# Revit family: Haworth_Planes_ConferenceDesk_Rectangle_AP_PRELIMINARY
name_source: partatom
category: Furniture
units: mm (PartAtom-declared; Revit-internal decimal feet)

## family parameters
Always vertical = Yes
Cut with Voids When Loaded = No
OmniClass Number = 23.40.70.14.64.21
OmniClass Title = Systems Furniture
Room Calculation Point = No
Shared = No
Work Plane-Based = No

## types (4) — shared parameters
Actual Height = 740 mm  [stored 2.42782 ft]
Assembly Code = E2020200
Description = Haworth - Planes - Conference Table - Rectangle
Flip Top Finish = Haworth _ Paint _ Undecided _ Table
Glide Finish = Haworth _ Polymer _ Black
Leg Height = 715 mm  [stored 2.3458 ft]
Manufacturer = Haworth
Model = WOPLTCR
Revision Number = 1
Size = Verify Final Dim. w/ Haworth
URL = https://www.haworth.com
URL - Product = https://www.haworth.com
Warranty = http://www.haworth.com

## per-type parameters (varying)
| type | Actual Depth | Actual Width | Flip Top | Large | Small |
| 1800w x 1000d | 1000 mm  [stored 3.28084 ft] | 1800 mm  [stored 5.90551 ft] | No | No | Yes |
| 1800w x 1200d | 1200 mm | 1800 mm  [stored 5.90551 ft] | Yes | No | Yes |
| 2000w x 1000d | 1000 mm  [stored 3.28084 ft] | 2000 mm  [stored 6.56168 ft] | Yes | Yes | No |
| 2000w x 1200d | 1200 mm | 2000 mm  [stored 6.56168 ft] | No | Yes | No |

note: [stored X ft] marks values corroborated as IEEE doubles in the binary element streams (Revit-internal decimal feet)

## geometry (parser evidence)
native form markers: Sweep x11
no freeform markers — native parametric forms only
